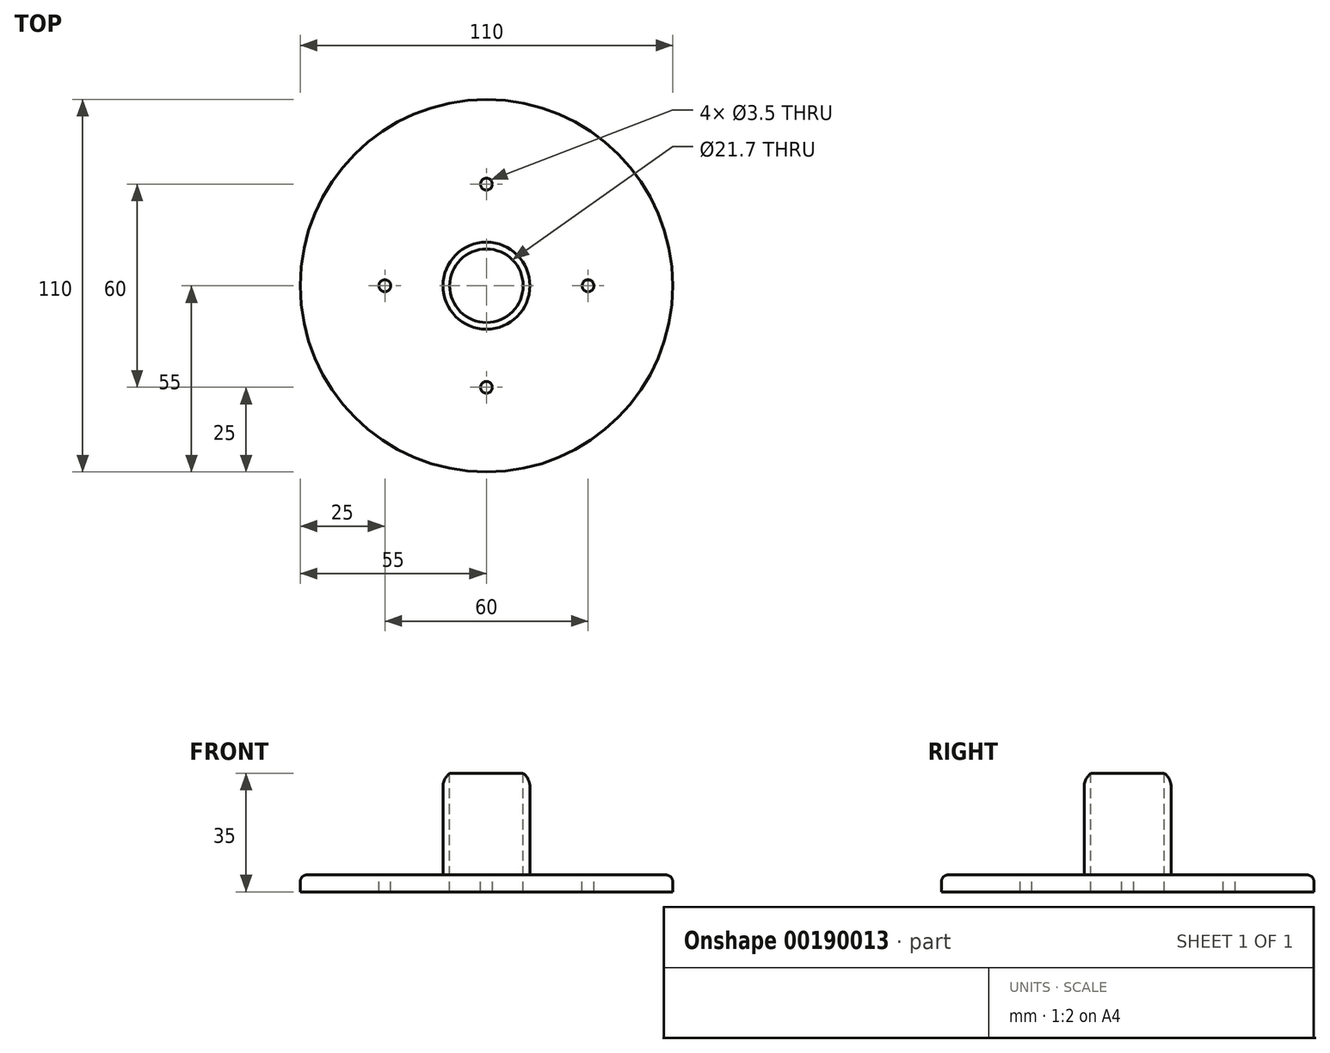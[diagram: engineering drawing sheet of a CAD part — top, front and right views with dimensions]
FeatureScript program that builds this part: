
annotation { "Feature Type Name" : "Feature", "Feature Type Description" : "" }
export const myFeature = defineFeature(function(context is Context, id is Id, definition is map)
    precondition{}
    {
        {
            var Q0;
            Q0=qCreatedBy(makeId("Top.planeOp"),FACE);
            var sketch = newSketch(context, id + "F0", { "sketchPlane" : qUnion([Q0])});
            skCircle(sketch, "E0", {"center": v(0, 0) * mm, "radius": 55 * mm});
            skSolve(sketch);
        }
        {
            var Q0;
            Q0=makeQuery(id+"F0.imprint","IMPRINT",FACE,{"disambiguationData":[TD([[makeQuery(id+"F0.imprint","IMPRINT",EDGE,{"derivedFrom":sQuery(id+"F0.wireOp",EDGE,"E0")}),1.0]])]});
            extrude(context, id + "F1", {"entities" : qUnion([Q0]), "depth" : 5 * mm});
        }
        {
            var Q0;
            Q0=makeQuery(id+"F1.opExtrude","CAP_FACE",FACE,{"disambiguationData":[OSD([sQuery(id+"F0.wireOp",EDGE,"E0")])],"isStart":false});
            var sketch = newSketch(context, id + "F2", { "sketchPlane" : qUnion([Q0])});
            skCircle(sketch, "E1", {"center": v(0, 0) * mm, "radius": 10.85 * mm});
            skSolve(sketch);
        }
        {
            var Q0;
            Q0 = qSketchRegion(id + "F2", true);
            extrude(context, id + "F3", {"entities" : qUnion([Q0]), "operationType" : NewBodyOperationType.REMOVE, "oppositeDirection" : true, "depth" : 25 * mm});
        }
        {
            var Q0;
            Q0=makeQuery(id+"F1.opExtrude","CAP_FACE",FACE,{"disambiguationData":[OSD([sQuery(id+"F0.wireOp",EDGE,"E0")])],"isStart":false});
            var sketch = newSketch(context, id + "F4", { "sketchPlane" : qUnion([Q0])});
            skCircle(sketch, "E2.0.0", {"center": v(0, 0) * mm, "radius": 55 * mm});
            skCircle(sketch, "E3", {"center": v(0, 0) * mm, "radius": 12.85 * mm});
            skSolve(sketch);
        }
        {
            var Q0;
            Q0=makeQuery(id+"F4.imprint","IMPRINT",FACE,{"disambiguationData":[TD([[makeQuery(id+"F4.imprint","IMPRINT",EDGE,{"derivedFrom":sQuery(id+"F4.wireOp",EDGE,"E3")}),1.0]])]});
            extrude(context, id + "F5", {"entities" : qUnion([Q0]), "operationType" : NewBodyOperationType.ADD, "depth" : 30 * mm});
        }
        {
            var Q0;
            Q0=makeQuery(id+"F5.opExtrude","CAP_EDGE",EDGE,{"disambiguationData":[OSD([sQuery(id+"F4.wireOp",EDGE,"E3")])],"isStart":false});
            fillet(context, id + "F6", {"entities" : qUnion([Q0]), "radius" : 5 * mm, "tangentPropagation" : true, "allowEdgeOverflow" : false});
        }
        {
            var Q0;
            Q0=makeQuery(id+"F1.opExtrude","CAP_EDGE",EDGE,{"disambiguationData":[OSD([sQuery(id+"F0.wireOp",EDGE,"E0")])],"isStart":false});
            fillet(context, id + "F7", {"entities" : qUnion([Q0]), "radius" : 2 * mm, "tangentPropagation" : true, "allowEdgeOverflow" : false});
        }
        {
            var Q0;
            Q0=makeQuery(id+"F1.opExtrude","CAP_FACE",FACE,{"disambiguationData":[OSD([sQuery(id+"F0.wireOp",EDGE,"E0")])],"isStart":false});
            var sketch = newSketch(context, id + "F8", { "sketchPlane" : qUnion([Q0])});
            skCircle(sketch, "E4", {"center": v(-30, 0) * mm, "radius": 1.75 * mm});
            skCircle(sketch, "E5.1.0", {"center": v(0, -30) * mm, "radius": 1.75 * mm});
            skCircle(sketch, "E5.2.0", {"center": v(30, 0) * mm, "radius": 1.75 * mm});
            skCircle(sketch, "E5.3.0", {"center": v(0, 30) * mm, "radius": 1.75 * mm});
            skPoint(sketch, "E5.center", {"position": v(0, 0) * mm});
            skSolve(sketch);
        }
        {
            var Q0;
            Q0 = qSketchRegion(id + "F8", true);
            extrude(context, id + "F9", {"entities" : qUnion([Q0]), "operationType" : NewBodyOperationType.REMOVE, "oppositeDirection" : true, "depth" : 25 * mm});
        }
    });
